# Revit family: PRD_FrankeWS_Hrdrrs_HeightAdjustment_ACDR0001-0005
name_source: partatom
category: Specialty Equipment
revit_build: Autodesk Revit 2018 (Build: 20190510_1515(x64)
units: mm (PartAtom-declared; Revit-internal decimal feet)

## family parameters
Cut with Voids When Loaded = No
Host = Face
OmniClass Number = 23.40.20.21.14
OmniClass Title = Hand and Hair Dryers
Part Type = Normal
Room Calculation Point = No
Round Connector Dimension = Use Diameter
Shared = No

## types (5) — shared parameters
AssetType = Fixed
BodyMaterial = PRD_AR_Aluminium
Category = Pr_40_70_62_36, Hairdryers
Default Elevation = 1800 mm  [stored 5.90551 ft]
DurationUnit = year
Features = height adjustment for F5 hood hair dryer, 600 mm continuously adjustable
Finish = coated
GrossWeight = 6.50 kg
IfcExportAs = IfcFurnitureType
IfcExportType = USERDEFINED
IsBuiltIn = TRUE
LeverMaterial = PRD_AR_Aluminium_Dark
MainColor = Silver
Manufacturer = KWC Group AG
ManufacturerName = KWC Group AG
ManufacturerURL = www.kwc.com
Material = Aluminium
NBSDescription = Hair dryers
NBSReference = 45-35-72/335
NetWeight = 5.80 kg
NominalDepth = 140 mm  [stored 0.459318 ft]
NominalHeight = 1210 mm  [stored 3.96982 ft]
NominalWidth = 250 mm  [stored 0.82021 ft]
ProductInformation = https://pim.kwc.com
Size = 250 x 1210 x 140 mm (W x H x D)
Style = Height adjustment
TailorMade = No
TypeOfMounting = Wall mounting
URL = www.kwc.com
Uniclass2015Code = Pr_40_70_62_36
Uniclass2015Title = Hairdryers
Uniclass2015Version = Products v1.17
Version = 1
WarrantyDurationUnit = year

## per-type parameters (varying)
| type | BIMObjectName | Color | ColorMaterial | Description | ModelNumber | Name |
| ACDR0001 | PRD_AR_Hairdryers_HeightAdjustment_ACDR0001 | White | PRD_AR_SyntheticWhite | Height adjustment for F5 hood hair dryer, for wall mounting, 600 mm continuously adjustable, with constant force rolling band spring, guide rail made of anodised aluminium, with 4 mm thick crystal mirror, fully adhered, covered, vandalism-resistant cable channel, colour combination silver/white end caps. | 2030052329 | Height adjustment ACDR0001 |
| ACDR0002 | PRD_AR_Hairdryers_HeightAdjustment_ACDR0002 | Basalt grey | PRD_AR_SyntheticBasaltGrey | Height adjustment for F5 hood hair dryer, for wall mounting, 600 mm continuously adjustable, with constant force rolling band spring, guide rail made of anodised aluminium, with 4 mm thick crystal mirror, fully adhered, covered, vandalism-resistant cable channel, colour combination silver/basalt grey end caps. | 2030052330 | Height adjustment ACDR0002 |
| ACDR0003 | PRD_AR_Hairdryers_HeightAdjustment_ACDR0003 | Pearl gentian blue | PRD_AR_SyntheticPearlGentianBlue | Height adjustment for F5 hood hair dryer, for wall mounting, 600 mm continuously adjustable, with constant force rolling band spring, guide rail made of anodised aluminium, with 4 mm thick crystal mirror, fully adhered, covered, vandalism-resistant cable channel, colour combination silver/pearl gentian blue end caps. | 2030052331 | Height adjustment ACDR0003 |
| ACDR0004 | PRD_AR_Hairdryers_HeightAdjustment_ACDR0004 | Lemon yellow | PRD_AR_SyntheticLemonYellow | Height adjustment for F5 hood hair dryer, for wall mounting, 600 mm continuously adjustable, with constant force rolling band spring, guide rail made of anodised aluminium, with 4 mm thick crystal mirror, fully adhered, covered, vandalism-resistant cable channel, colour combination silver/lemon yellow end caps. | 2030052332 | Height adjustment ACDR0004 |
| ACDR0005 | PRD_AR_Hairdryers_HeightAdjustment_ACDR0005 | Signal red | PRD_AR_SyntheticSignalRed | Height adjustment for F5 hood hair dryer, for wall mounting, 600 mm continuously adjustable, with constant force rolling band spring, guide rail made of anodised aluminium, with 4 mm thick crystal mirror, fully adhered, covered, vandalism-resistant cable channel, colour combination silver/signal red end caps. | 2030052333 | Height adjustment ACDR0005 |

note: column(s) folded — value = type name in every type: Model, ModelReference

note: [stored X ft] marks values corroborated as IEEE doubles in the binary element streams (Revit-internal decimal feet)

## geometry (parser evidence)
native form markers: Sweep x6
no freeform markers — native parametric forms only
